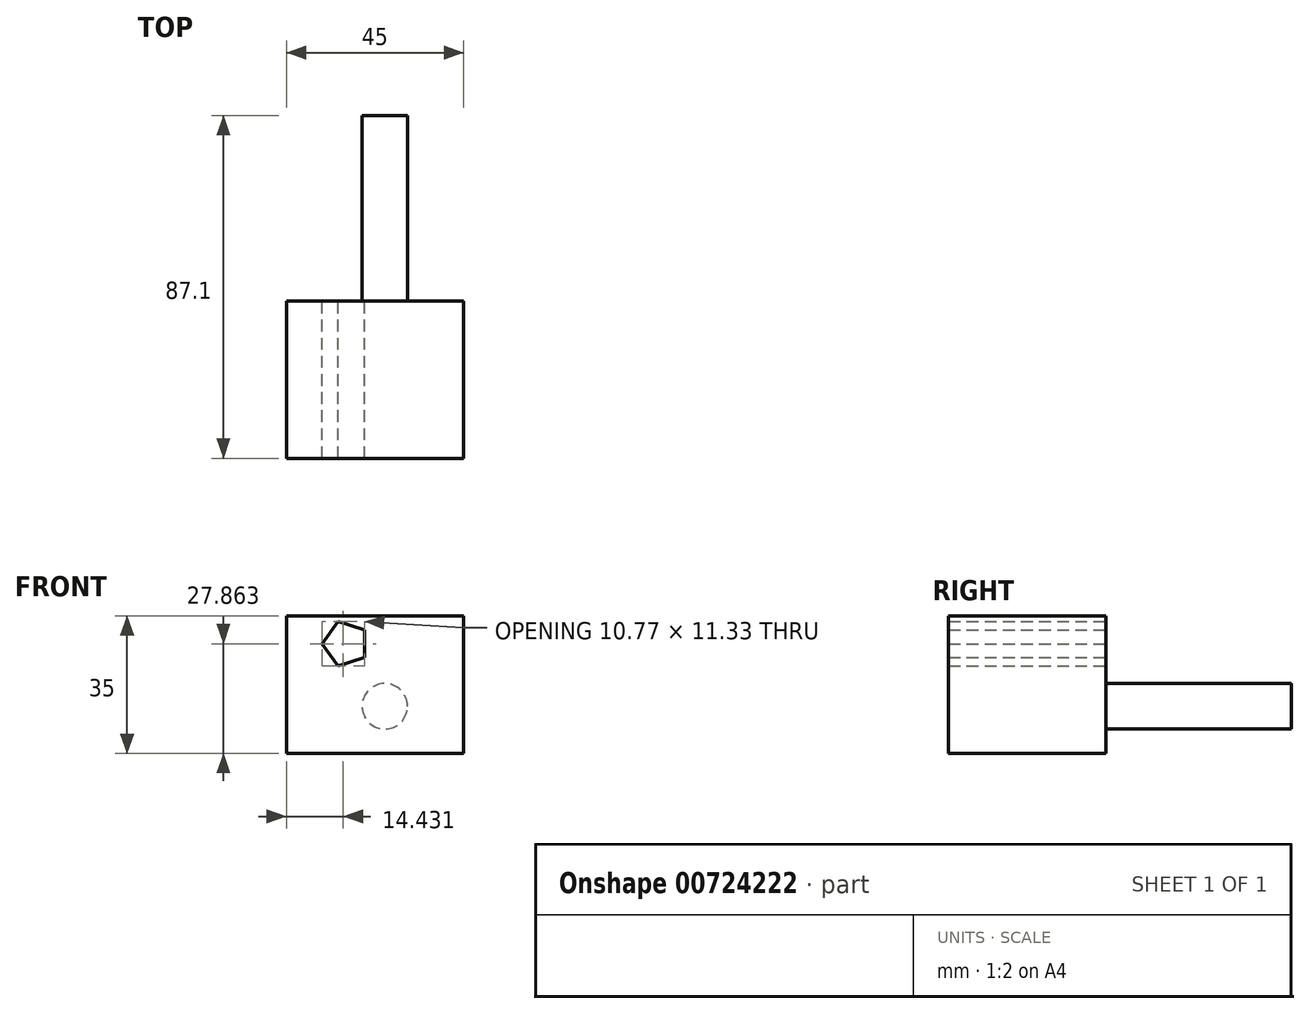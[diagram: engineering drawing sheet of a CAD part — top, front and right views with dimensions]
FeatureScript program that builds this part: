
annotation { "Feature Type Name" : "Feature", "Feature Type Description" : "" }
export const myFeature = defineFeature(function(context is Context, id is Id, definition is map)
    precondition{}
    {
        {
            var Q0;
            Q0=qCreatedBy(makeId("Front.planeOp"),FACE);
            var sketch = newSketch(context, id + "F0", { "sketchPlane" : qUnion([Q0])});
            skLineSegment(sketch, "E0.bottom", {"start": v(0, 0) * mm, "end": v(-45, 0) * mm});
            skLineSegment(sketch, "E0.top", {"start": v(0, 35) * mm, "end": v(-45, 35) * mm});
            skLineSegment(sketch, "E0.left", {"start": v(0, 0) * mm, "end": v(0, 35) * mm});
            skLineSegment(sketch, "E0.right", {"start": v(-45, 0) * mm, "end": v(-45, 35) * mm});
            skCircle(sketch, "E1.cCircle", {"center": v(-30, 27.86) * mm, "radius": 4.82 * mm, "construction": true});
            skLineSegment(sketch, "E1.0", {"start": v(-25.18, 31.36) * mm, "end": v(-25.18, 24.36) * mm});
            skLineSegment(sketch, "E1.1", {"start": v(-25.18, 24.36) * mm, "end": v(-31.84, 22.2) * mm});
            skLineSegment(sketch, "E1.2", {"start": v(-31.84, 22.2) * mm, "end": v(-35.95, 27.86) * mm});
            skLineSegment(sketch, "E1.3", {"start": v(-35.95, 27.86) * mm, "end": v(-31.84, 33.53) * mm});
            skLineSegment(sketch, "E1.4", {"start": v(-31.84, 33.53) * mm, "end": v(-25.18, 31.36) * mm});
            skPoint(sketch, "E1.0.midPoint", {"position": v(-25.18, 27.86) * mm});
            skSolve(sketch);
        }
        {
            var Q0;
            Q0=makeQuery(id+"F0.imprint","IMPRINT",FACE,{"disambiguationData":[TD([[makeQuery(id+"F0.imprint","IMPRINT",EDGE,{"derivedFrom":sQuery(id+"F0.wireOp",EDGE,"E0.bottom")}),-1.0]])]});
            extrude(context, id + "F1", {"entities" : qUnion([Q0]), "depth" : 40 * mm, "offsetDistance" : 25 * mm});
        }
        {
            var Q0;
            Q0=makeQuery(id+"F1.opExtrude","CAP_FACE",FACE,{"disambiguationData":[OSD([sQuery(id+"F0.wireOp",EDGE,"E0.bottom"),sQuery(id+"F0.wireOp",EDGE,"E0.top"),sQuery(id+"F0.wireOp",EDGE,"E0.left"),sQuery(id+"F0.wireOp",EDGE,"E0.right"),sQuery(id+"F0.wireOp",EDGE,"E1.0"),sQuery(id+"F0.wireOp",EDGE,"E1.1"),sQuery(id+"F0.wireOp",EDGE,"E1.2"),sQuery(id+"F0.wireOp",EDGE,"E1.3"),sQuery(id+"F0.wireOp",EDGE,"E1.4")])],"isStart":true});
            var sketch = newSketch(context, id + "F2", { "sketchPlane" : qUnion([Q0])});
            skCircle(sketch, "E2", {"center": v(20, 12) * mm, "radius": 5.78 * mm});
            skSolve(sketch);
        }
        {
            var Q0;
            Q0 = qSketchRegion(id + "F2", true);
            extrude(context, id + "F3", {"entities" : qUnion([Q0]), "operationType" : NewBodyOperationType.ADD, "depth" : 47.1 * mm, "offsetDistance" : 25 * mm});
        }
    });
